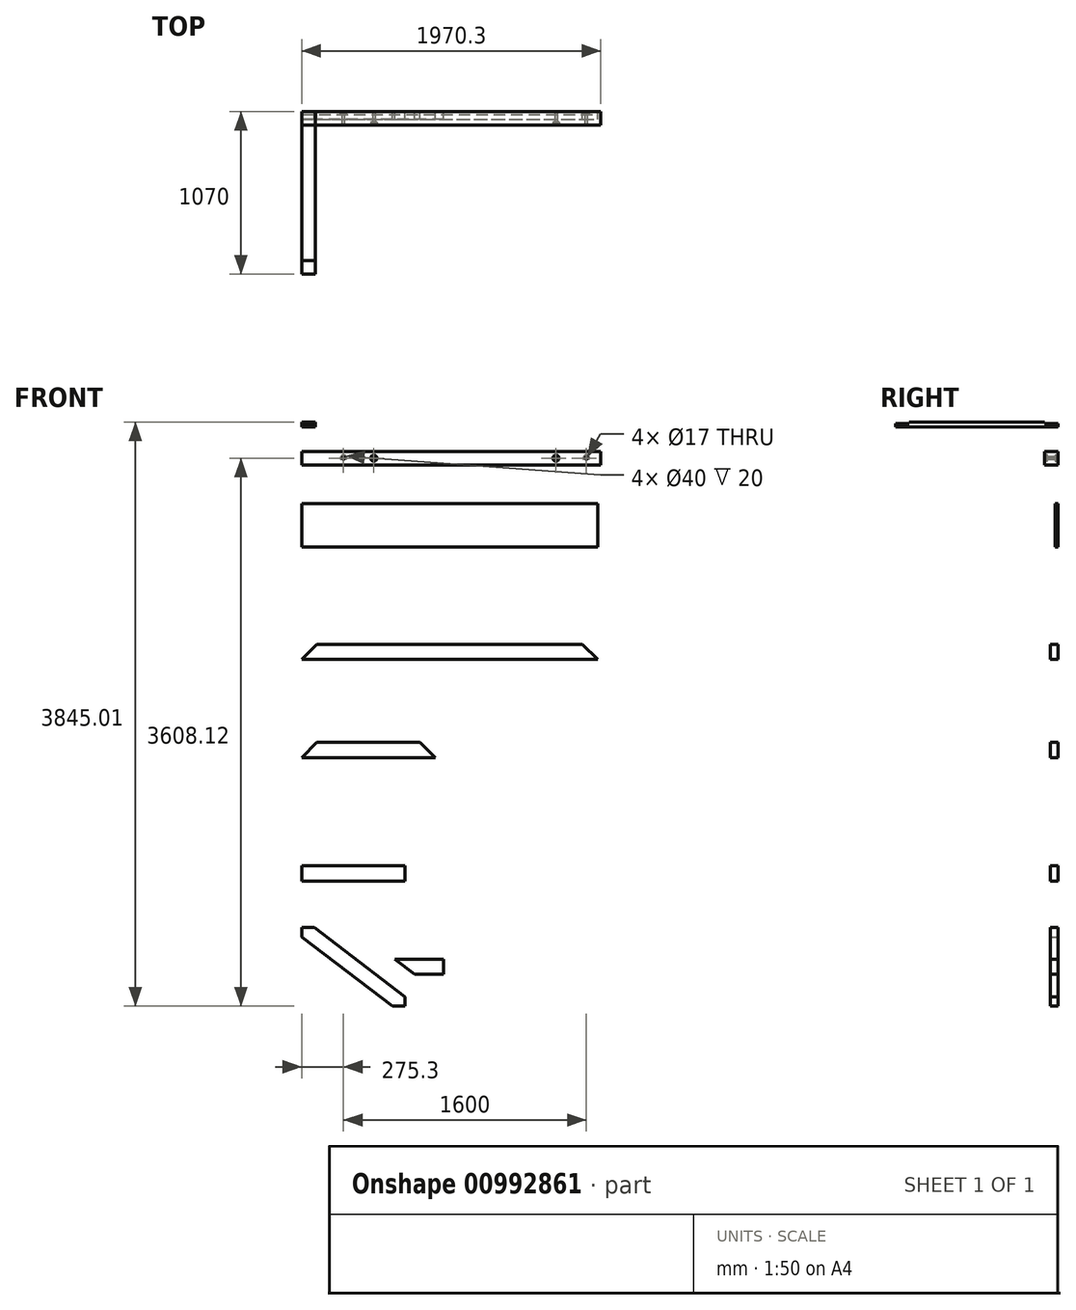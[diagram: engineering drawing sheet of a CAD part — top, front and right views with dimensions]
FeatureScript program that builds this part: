
annotation { "Feature Type Name" : "Feature", "Feature Type Description" : "" }
export const myFeature = defineFeature(function(context is Context, id is Id, definition is map)
    precondition{}
    {
        {
            var Q0;
            Q0=qCreatedBy(makeId("Front.planeOp"),FACE);
            var sketch = newSketch(context, id + "F0", { "sketchPlane" : qUnion([Q0])});
            skLineSegment(sketch, "E0.bottom", {"start": v(0, 0) * mm, "end": v(1970, 0) * mm});
            skLineSegment(sketch, "E0.top", {"start": v(0, 90) * mm, "end": v(1970, 90) * mm});
            skLineSegment(sketch, "E0.left", {"start": v(0, 0) * mm, "end": v(0, 90) * mm});
            skLineSegment(sketch, "E1", {"start": v(1970, 90) * mm, "end": v(1970, 0) * mm});
            skSolve(sketch);
        }
        {
            var Q0;
            Q0 = qSketchRegion(id + "F0", true);
            extrude(context, id + "F1", {"entities" : qUnion([Q0]), "depth" : 90 * mm, "offsetDistance" : 25 * mm});
        }
        {
            var Q0;
            Q0=qCreatedBy(makeId("Right.planeOp"),FACE);
            var sketch = newSketch(context, id + "F2", { "sketchPlane" : qUnion([Q0])});
            skLineSegment(sketch, "E2.bottom", {"start": v(0, 251.9) * mm, "end": v(-1070, 251.9) * mm});
            skLineSegment(sketch, "E2.top", {"start": v(0, 271.9) * mm, "end": v(-90, 271.9) * mm});
            skLineSegment(sketch, "E2.left", {"start": v(0, 251.9) * mm, "end": v(0, 271.9) * mm});
            skLineSegment(sketch, "E2.right", {"start": v(-1070, 251.9) * mm, "end": v(-1070, 271.9) * mm});
            skLineSegment(sketch, "E3", {"start": v(-90, 271.9) * mm, "end": v(-90, 281.9) * mm});
            skLineSegment(sketch, "E4", {"start": v(-90, 281.9) * mm, "end": v(-980, 281.9) * mm});
            skLineSegment(sketch, "E5", {"start": v(-980, 281.9) * mm, "end": v(-980, 271.9) * mm});
            skLineSegment(sketch, "E6.trimOffspring", {"start": v(-980, 271.9) * mm, "end": v(-1070, 271.9) * mm});
            skSolve(sketch);
        }
        {
            var Q0;
            Q0 = qSketchRegion(id + "F2", true);
            extrude(context, id + "F3", {"entities" : qUnion([Q0]), "depth" : 90 * mm, "offsetDistance" : 25 * mm});
        }
        {
            var Q0;
            Q0=qCreatedBy(makeId("Front.planeOp"),FACE);
            var sketch = newSketch(context, id + "F4", { "sketchPlane" : qUnion([Q0])});
            skLineSegment(sketch, "E7.bottom", {"start": v(-0.3, -253.95) * mm, "end": v(1949.7, -253.95) * mm});
            skLineSegment(sketch, "E7.top", {"start": v(-0.3, -538.95) * mm, "end": v(1949.7, -538.95) * mm});
            skLineSegment(sketch, "E7.left", {"start": v(-0.3, -253.95) * mm, "end": v(-0.3, -538.95) * mm});
            skLineSegment(sketch, "E7.right", {"start": v(1949.7, -253.95) * mm, "end": v(1949.7, -538.95) * mm});
            skLineSegment(sketch, "E8.bottom", {"start": v(99.7, -1181.3) * mm, "end": v(1849.7, -1181.3) * mm});
            skLineSegment(sketch, "E8.top", {"start": v(-0.3, -1281.3) * mm, "end": v(1949.7, -1281.3) * mm});
            skLineSegment(sketch, "E9", {"start": v(99.7, -1181.3) * mm, "end": v(-0.3, -1281.3) * mm});
            skLineSegment(sketch, "E10", {"start": v(1849.7, -1181.3) * mm, "end": v(1949.7, -1281.3) * mm});
            skLineSegment(sketch, "E11.bottom", {"start": v(99.93, -1826.07) * mm, "end": v(779.93, -1826.07) * mm});
            skLineSegment(sketch, "E11.top", {"start": v(-0.07, -1926.07) * mm, "end": v(879.93, -1926.07) * mm});
            skLineSegment(sketch, "E12", {"start": v(99.93, -1826.07) * mm, "end": v(-0.07, -1926.07) * mm});
            skLineSegment(sketch, "E13", {"start": v(779.93, -1826.07) * mm, "end": v(879.93, -1926.07) * mm});
            skPoint(sketch, "E14.orphan", {"position": v(0, -1826.07) * mm});
            skLineSegment(sketch, "E15.bottom", {"start": v(0, -2639.24) * mm, "end": v(680, -2639.24) * mm});
            skLineSegment(sketch, "E15.top", {"start": v(0, -2739.24) * mm, "end": v(680, -2739.24) * mm});
            skLineSegment(sketch, "E15.left", {"start": v(0, -2639.24) * mm, "end": v(0, -2739.24) * mm});
            skLineSegment(sketch, "E15.right", {"start": v(680, -2639.24) * mm, "end": v(680, -2739.24) * mm});
            skLineSegment(sketch, "E16.bottom", {"start": v(0, -3046.12) * mm, "end": v(83.2, -3046.12) * mm});
            skLineSegment(sketch, "E16.top", {"start": v(597.39, -3563.12) * mm, "end": v(680, -3563.12) * mm});
            skLineSegment(sketch, "E16.left", {"start": v(0, -3046.12) * mm, "end": v(0, -3108.93) * mm});
            skLineSegment(sketch, "E16.right", {"start": v(680, -3500.84) * mm, "end": v(680, -3563.12) * mm});
            skLineSegment(sketch, "E17", {"start": v(83.2, -3046.12) * mm, "end": v(488.1, -3354.62) * mm});
            skLineSegment(sketch, "E18", {"start": v(597.39, -3563.12) * mm, "end": v(0, -3108.93) * mm});
            skPoint(sketch, "E19.start.orphan", {"position": v(340, -3304.62) * mm});
            skLineSegment(sketch, "E20.bottom", {"start": v(935.54, -3254.62) * mm, "end": v(612.39, -3254.62) * mm});
            skLineSegment(sketch, "E20.top", {"start": v(935.54, -3354.62) * mm, "end": v(743.63, -3354.62) * mm});
            skLineSegment(sketch, "E20.left", {"start": v(935.54, -3254.62) * mm, "end": v(935.54, -3354.62) * mm});
            skPoint(sketch, "E20.right.end.orphan", {"position": v(0, -3354.62) * mm});
            skPoint(sketch, "E20.right.start.orphan", {"position": v(0, -3254.62) * mm});
            skLineSegment(sketch, "E21", {"start": v(612.39, -3254.62) * mm, "end": v(743.63, -3354.62) * mm});
            skLineSegment(sketch, "E22.trimOffspring", {"start": v(488.1, -3354.62) * mm, "end": v(680, -3500.84) * mm});
            skSolve(sketch);
        }
        {
            var Q0;
            Q0=makeQuery(id+"F4.imprint","IMPRINT",FACE,{"disambiguationData":[TD([[makeQuery(id+"F4.imprint","IMPRINT",EDGE,{"derivedFrom":sQuery(id+"F4.wireOp",EDGE,"E7.bottom")}),-1.0]])]});
            extrude(context, id + "F5", {"entities" : qUnion([Q0]), "depth" : 20 * mm, "offsetDistance" : 25 * mm});
        }
        {
            var Q0;
            Q0=makeQuery(id+"F4.imprint","IMPRINT",FACE,{"disambiguationData":[TD([[makeQuery(id+"F4.imprint","IMPRINT",EDGE,{"derivedFrom":sQuery(id+"F4.wireOp",EDGE,"E8.bottom")}),-1.0]])]});
            extrude(context, id + "F6", {"entities" : qUnion([Q0]), "depth" : 50 * mm, "offsetDistance" : 25 * mm});
        }
        {
            var Q0;
            Q0=makeQuery(id+"F4.imprint","IMPRINT",FACE,{"disambiguationData":[TD([[makeQuery(id+"F4.imprint","IMPRINT",EDGE,{"derivedFrom":sQuery(id+"F4.wireOp",EDGE,"E11.bottom")}),-1.0]])]});
            extrude(context, id + "F7", {"entities" : qUnion([Q0]), "depth" : 50 * mm, "offsetDistance" : 25 * mm});
        }
        {
            var Q0;
            Q0=makeQuery(id+"F4.imprint","IMPRINT",FACE,{"disambiguationData":[TD([[makeQuery(id+"F4.imprint","IMPRINT",EDGE,{"derivedFrom":sQuery(id+"F4.wireOp",EDGE,"E15.bottom")}),-1.0]])]});
            extrude(context, id + "F8", {"entities" : qUnion([Q0]), "depth" : 50 * mm, "offsetDistance" : 25 * mm});
        }
        {
            var Q0;
            Q0=makeQuery(id+"F4.imprint","IMPRINT",FACE,{"disambiguationData":[TD([[makeQuery(id+"F4.imprint","IMPRINT",EDGE,{"derivedFrom":sQuery(id+"F4.wireOp",EDGE,"E16.bottom")}),-1.0]])]});
            extrude(context, id + "F9", {"entities" : qUnion([Q0]), "depth" : 25 * mm, "offsetDistance" : 25 * mm});
        }
        {
            var Q0;
            Q0=makeQuery(id+"F4.imprint","IMPRINT",FACE,{"disambiguationData":[TD([[makeQuery(id+"F4.imprint","IMPRINT",EDGE,{"derivedFrom":sQuery(id+"F4.wireOp",EDGE,"E16.bottom")}),-1.0]])]});
            extrude(context, id + "F10", {"entities" : qUnion([Q0]), "operationType" : NewBodyOperationType.ADD, "depth" : 50 * mm, "offsetDistance" : 25 * mm});
        }
        {
            var Q0;
            Q0=makeQuery(id+"F1.opExtrude","CAP_FACE",FACE,{"disambiguationData":[OSD([sQuery(id+"F0.wireOp",EDGE,"E0.bottom"),sQuery(id+"F0.wireOp",EDGE,"E0.top"),sQuery(id+"F0.wireOp",EDGE,"E0.left"),sQuery(id+"F0.wireOp",EDGE,"E1")])],"isStart":false});
            cPlane(context, id + "F11", {"entities" : qUnion([Q0]), "cplaneType" : CPlaneType.OFFSET, "offset" : 25 * mm, "width" : 150 * mm, "height" : 150 * mm});
        }
        {
            var Q0;
            Q0=qCreatedBy(id+"F11.planeOp",FACE);
            var sketch = newSketch(context, id + "F12", { "sketchPlane" : qUnion([Q0])});
            skLineSegment(sketch, "E23", {"start": v(1969.9, 0) * mm, "end": v(1969.9, 45) * mm});
            skLineSegment(sketch, "E24", {"start": v(1969.9, 45) * mm, "end": v(1969.9, 45) * mm});
            skLineSegment(sketch, "E25", {"start": v(1969.9, 45) * mm, "end": v(1674.9, 45) * mm});
            skLineSegment(sketch, "E26", {"start": v(1674.9, 45) * mm, "end": v(474.9, 45) * mm});
            skSolve(sketch);
        }
        {
            var Q0;
            Q0=sQuery(id+"F12.wireOp",VERTEX,"E25.end");
            var Q1;
            Q1=sQuery(id+"F12.wireOp",VERTEX,"E26.end");
            var Q2;
            Q2=makeQuery(id+"F1.opExtrude","SWEPT_BODY",BODY,{"disambiguationData":[OSD([sQuery(id+"F0.wireOp",EDGE,"E0.bottom"),sQuery(id+"F0.wireOp",EDGE,"E0.top"),sQuery(id+"F0.wireOp",EDGE,"E0.left"),sQuery(id+"F0.wireOp",EDGE,"E1")])]});
            hole(context, id + "F13", {"style" : HoleStyle.C_BORE, "endStyle" : HoleEndStyle.BLIND, "holeDiameter" : 17 * mm, "cBoreDiameter" : 40 * mm, "cBoreDepth" : 20 * mm, "majorDiameter" : 5 * mm, "holeDepth" : 100 * mm, "isTappedThrough" : true, "tappedDepth" : 12 * mm, "tapClearance" : 3, "locations" : qUnion([Q0, Q1]), "scope" : qUnion([Q2])});
        }
        {
            var Q0;
            Q0=makeQuery(id+"F1.opExtrude","CAP_FACE",FACE,{"disambiguationData":[OSD([sQuery(id+"F0.wireOp",EDGE,"E0.bottom"),sQuery(id+"F0.wireOp",EDGE,"E0.top"),sQuery(id+"F0.wireOp",EDGE,"E0.left"),sQuery(id+"F0.wireOp",EDGE,"E1")])],"isStart":true});
            var sketch = newSketch(context, id + "F14", { "sketchPlane" : qUnion([Q0])});
            skLineSegment(sketch, "E27", {"start": v(-1970, 90) * mm, "end": v(-1970, 45) * mm});
            skLineSegment(sketch, "E28", {"start": v(-1970, 45) * mm, "end": v(-1875, 45) * mm});
            skLineSegment(sketch, "E29", {"start": v(-1875, 45) * mm, "end": v(-275, 45) * mm});
            skSolve(sketch);
        }
        {
            var Q0;
            Q0=sQuery(id+"F14.wireOp",VERTEX,"E28.end");
            var Q1;
            Q1=sQuery(id+"F14.wireOp",VERTEX,"E29.end");
            var Q2;
            Q2=makeQuery(id+"F1.opExtrude","SWEPT_BODY",BODY,{"disambiguationData":[OSD([sQuery(id+"F0.wireOp",EDGE,"E0.bottom"),sQuery(id+"F0.wireOp",EDGE,"E0.top"),sQuery(id+"F0.wireOp",EDGE,"E0.left"),sQuery(id+"F0.wireOp",EDGE,"E1")])]});
            hole(context, id + "F15", {"style" : HoleStyle.C_BORE, "endStyle" : HoleEndStyle.BLIND, "holeDiameter" : 17 * mm, "cBoreDiameter" : 40 * mm, "cBoreDepth" : 20 * mm, "majorDiameter" : 5 * mm, "holeDepth" : 100 * mm, "isTappedThrough" : true, "tappedDepth" : 12 * mm, "tapClearance" : 3, "locations" : qUnion([Q0, Q1]), "scope" : qUnion([Q2])});
        }
        {
            var Q0;
            Q0=makeQuery(id+"F4.imprint","IMPRINT",FACE,{"disambiguationData":[TD([[makeQuery(id+"F4.imprint","IMPRINT",EDGE,{"derivedFrom":sQuery(id+"F4.wireOp",EDGE,"E20.bottom")}),1.0]])]});
            extrude(context, id + "F16", {"entities" : qUnion([Q0]), "depth" : 50 * mm, "offsetDistance" : 25 * mm});
        }
    });
